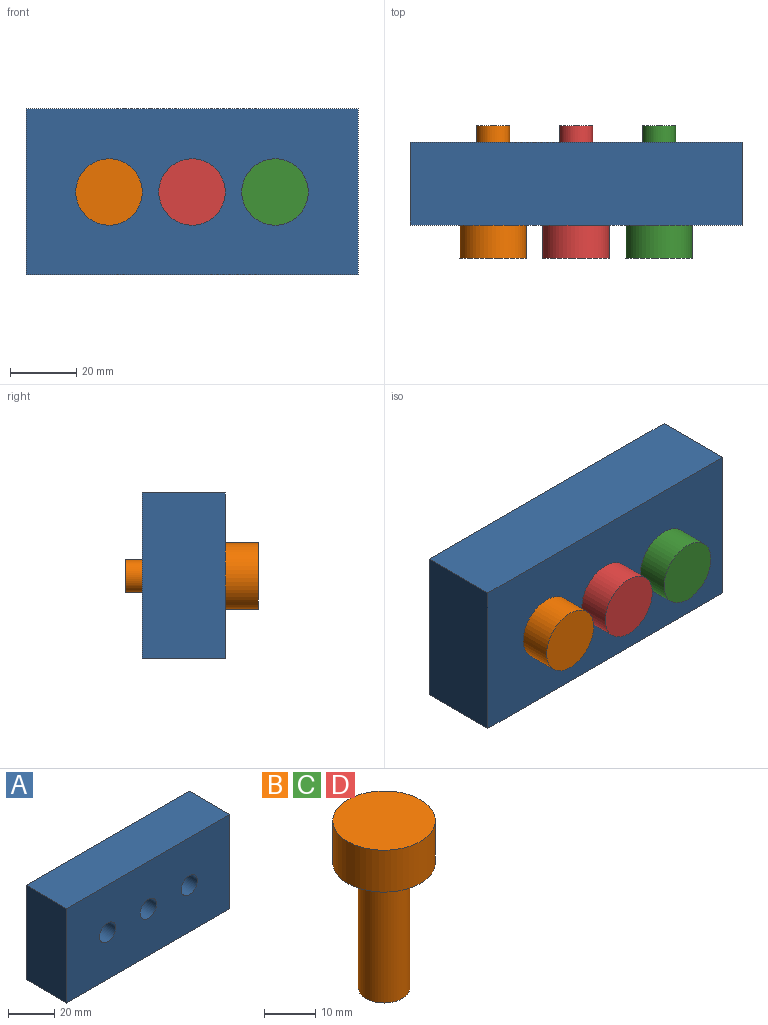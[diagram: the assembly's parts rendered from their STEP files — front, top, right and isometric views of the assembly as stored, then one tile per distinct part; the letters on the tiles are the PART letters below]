
ASSEMBLY  parts=4 mates=1
PART A: 9 faces, bbox 100x25x50 mm
  f0: plane 50x25mm, normal (-1,0,0), area 1250mm2, adj f1,f5,f7,f8
  f1: plane 100x25mm, normal (0,0,-1), area 2500mm2, adj f0,f2,f7,f8
  f2: plane 50x25mm, normal (1,0,0), area 1250mm2, adj f1,f5,f7,f8
  f3: cylinder r=5mm len=25mm, axis (0,1,0), area 785.4mm2, adj f7,f8
  f4: cylinder r=5mm len=25mm, axis (0,1,0), area 785.4mm2, adj f7,f8
  f5: plane 100x25mm, normal (0,0,1), area 2500mm2, adj f0,f2,f7,f8
  f6: cylinder r=5mm len=25mm, axis (0,1,0), area 785.4mm2, adj f7,f8
  f7: plane 100x50mm, normal (0,-1,0), area 4764.4mm2, adj f0,f1,f2,f3,f4,f5,f6
  f8: plane 100x50mm, normal (0,1,0), area 4764.4mm2, adj f0,f1,f2,f3,f4,f5,f6
PART B: 5 faces, bbox 20x20x40 mm
  f0: plane 10x10mm, normal (0,0,-1), area 78.5mm2, adj f1
  f1: cylinder r=5mm len=30mm, axis (0,0,1), area 942.5mm2, adj f0,f2
  f2: plane 20x20mm, normal (0,0,-1), area 235.6mm2, adj f1,f3
  f3: cylinder r=10mm len=20mm, axis (0,0,1), area 628.3mm2, adj f2,f4
  f4: plane 20x20mm, normal (0,0,1), area 314.2mm2, adj f3
PART C: same geometry as B
PART D: same geometry as B
PLACE A t=(-49.69,12.4,-25.42)mm fixed
PLACE B rot(axis=(1,0,0),90deg) t=(-24.69,17.4,-0.42)mm
PLACE C rot(axis=(1,0,0),90deg) t=(25.31,17.4,-0.42)mm
PLACE D rot(axis=(1,0,0),90deg) t=(0.31,17.4,-0.42)mm
MATE revolute B.f1 <-> A.f4  axis (0,-1,0) through (-24.69,-12.6,-0.42)mm
